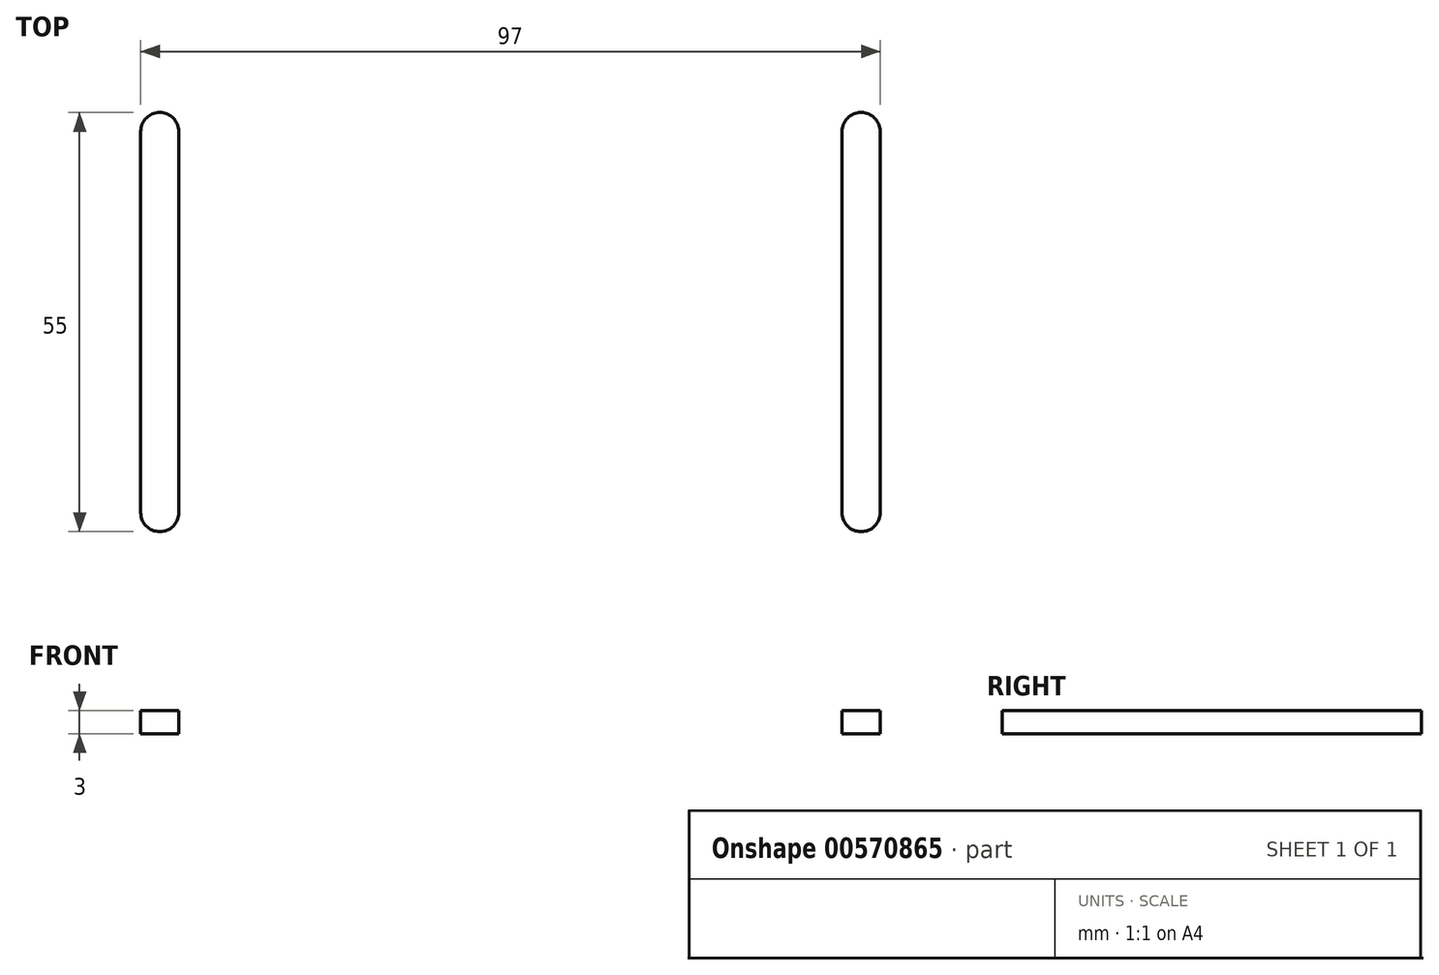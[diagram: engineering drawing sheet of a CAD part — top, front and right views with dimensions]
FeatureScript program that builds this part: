
annotation { "Feature Type Name" : "Feature", "Feature Type Description" : "" }
export const myFeature = defineFeature(function(context is Context, id is Id, definition is map)
    precondition{}
    {
        {
            var Q0;
            Q0=qCreatedBy(makeId("Top.planeOp"),FACE);
            var sketch = newSketch(context, id + "F0", { "sketchPlane" : qUnion([Q0])});
            skLineSegment(sketch, "E0.bottom", {"start": v(0, 0) * mm, "end": v(56, 0) * mm});
            skLineSegment(sketch, "E0.top", {"start": v(0, 145) * mm, "end": v(56, 145) * mm});
            skLineSegment(sketch, "E0.left", {"start": v(0, 0) * mm, "end": v(0, 145) * mm});
            skLineSegment(sketch, "E0.right", {"start": v(56, 0) * mm, "end": v(56, 145) * mm});
            skSolve(sketch);
        }
        {
            var Q0;
            Q0=makeQuery(id+"F0.imprint","IMPRINT",FACE,{"disambiguationData":[TD([[makeQuery(id+"F0.imprint","IMPRINT",EDGE,{"derivedFrom":sQuery(id+"F0.wireOp",EDGE,"E0.bottom")}),1.0]])]});
            extrude(context, id + "F1", {"entities" : qUnion([Q0]), "depth" : 3 * mm, "offsetDistance" : 25 * mm});
        }
        {
            var Q0;
            Q0=makeQuery(id+"F1.opExtrude","CAP_FACE",FACE,{"disambiguationData":[OSD([sQuery(id+"F0.wireOp",EDGE,"E0.bottom"),sQuery(id+"F0.wireOp",EDGE,"E0.top"),sQuery(id+"F0.wireOp",EDGE,"E0.left"),sQuery(id+"F0.wireOp",EDGE,"E0.right")])],"isStart":false});
            var sketch = newSketch(context, id + "F2", { "sketchPlane" : qUnion([Q0])});
            skLineSegment(sketch, "E1", {"start": v(25, 69) * mm, "end": v(25, 45) * mm});
            skSolve(sketch);
        }
        {
            var Q0;
            Q0=sQuery(id+"F2.wireOp",VERTEX,"E1.start");
            var Q1;
            Q1=sQuery(id+"F2.wireOp",VERTEX,"E1.end");
            var Q2;
            Q2=makeQuery(id+"F1.opExtrude","SWEPT_BODY",BODY,{"disambiguationData":[OSD([sQuery(id+"F0.wireOp",EDGE,"E0.bottom"),sQuery(id+"F0.wireOp",EDGE,"E0.top"),sQuery(id+"F0.wireOp",EDGE,"E0.left"),sQuery(id+"F0.wireOp",EDGE,"E0.right")])]});
            hole(context, id + "F3", {"style" : HoleStyle.SIMPLE, "endStyle" : HoleEndStyle.THROUGH, "holeDiameter" : 3 * mm, "isTappedThrough" : true, "tappedDepth" : 12 * mm, "tapClearance" : 3, "locations" : qUnion([Q0, Q1]), "scope" : qUnion([Q2])});
        }
        {
            var Q0;
            Q0=makeQuery(id+"F1.opExtrude","CAP_FACE",FACE,{"disambiguationData":[OSD([sQuery(id+"F0.wireOp",EDGE,"E0.bottom"),sQuery(id+"F0.wireOp",EDGE,"E0.top"),sQuery(id+"F0.wireOp",EDGE,"E0.left"),sQuery(id+"F0.wireOp",EDGE,"E0.right")])],"isStart":false});
            var sketch = newSketch(context, id + "F4", { "sketchPlane" : qUnion([Q0])});
            skLineSegment(sketch, "E2", {"start": v(36.35, 48.6) * mm, "end": v(36.35, 104.74) * mm});
            skSolve(sketch);
        }
        {
            var Q0;
            Q0=makeQuery(id+"F4.imprint","IMPRINT",FACE,{"disambiguationData":[TD([[makeQuery(id+"F4.imprint","IMPRINT",EDGE,{"derivedFrom":makeQuery(id+"F1.opExtrude","CAP_EDGE",EDGE,{"disambiguationData":[OSD([sQuery(id+"F0.wireOp",EDGE,"E0.bottom")])],"isStart":false})}),1.0]])]});
            var sketch = newSketch(context, id + "F5", { "sketchPlane" : qUnion([Q0])});
            skLineSegment(sketch, "E3", {"start": v(46, 82) * mm, "end": v(46, 32) * mm});
            skSolve(sketch);
        }
        {
            var Q0;
            Q0=makeQuery(id+"F5.imprint","IMPRINT",FACE,{"disambiguationData":[TD([[makeQuery(id+"F5.imprint","IMPRINT",EDGE,{"derivedFrom":makeQuery(id+"F4.imprint","IMPRINT",EDGE,{"derivedFrom":makeQuery(id+"F1.opExtrude","CAP_EDGE",EDGE,{"disambiguationData":[OSD([sQuery(id+"F0.wireOp",EDGE,"E0.bottom")])],"isStart":false})})}),1.0]])]});
            var sketch = newSketch(context, id + "F6", { "sketchPlane" : qUnion([Q0])});
            skSolve(sketch);
        }
        {
            var Q0;
            Q0=makeQuery(id+"F5.imprint","IMPRINT",FACE,{"disambiguationData":[TD([[makeQuery(id+"F5.imprint","IMPRINT",EDGE,{"derivedFrom":makeQuery(id+"F4.imprint","IMPRINT",EDGE,{"derivedFrom":makeQuery(id+"F1.opExtrude","CAP_EDGE",EDGE,{"disambiguationData":[OSD([sQuery(id+"F0.wireOp",EDGE,"E0.bottom")])],"isStart":false})})}),1.0]])]});
            var sketch = newSketch(context, id + "F7", { "sketchPlane" : qUnion([Q0])});
            skLineSegment(sketch, "E4.JWB.JWB", {"start": v(46, 82) * mm, "end": v(46, 32) * mm, "construction": true});
            skArc(sketch, "E4.0.startCap", {"start": v(43.5, 82) * mm, "mid": v(46, 84.5) * mm, "end": v(48.5, 82) * mm});
            skArc(sketch, "E4.0.endCap", {"start": v(48.5, 32) * mm, "mid": v(46, 29.5) * mm, "end": v(43.5, 32) * mm});
            skLineSegment(sketch, "E4.0.left", {"start": v(48.5, 82) * mm, "end": v(48.5, 32) * mm});
            skLineSegment(sketch, "E4.0.right", {"start": v(43.5, 82) * mm, "end": v(43.5, 32) * mm});
            skSolve(sketch);
        }
        {
            var Q0;
            Q0=makeQuery(id+"F7.imprint","IMPRINT",FACE,{"disambiguationData":[TD([[makeQuery(id+"F7.imprint","IMPRINT",EDGE,{"derivedFrom":sQuery(id+"F7.wireOp",EDGE,"E4.0.startCap")}),-1.0]])]});
            extrude(context, id + "F8", {"entities" : qUnion([Q0]), "operationType" : NewBodyOperationType.REMOVE, "oppositeDirection" : true, "depth" : 25 * mm, "offsetDistance" : 25 * mm});
        }
        {
            var Q0;
            Q0=makeQuery(id+"F6.imprint","IMPRINT",FACE,{"disambiguationData":[TD([[makeQuery(id+"F6.imprint","IMPRINT",EDGE,{"derivedFrom":makeQuery(id+"F5.imprint","IMPRINT",EDGE,{"derivedFrom":makeQuery(id+"F4.imprint","IMPRINT",EDGE,{"derivedFrom":makeQuery(id+"F1.opExtrude","CAP_EDGE",EDGE,{"disambiguationData":[OSD([sQuery(id+"F0.wireOp",EDGE,"E0.bottom")])],"isStart":false})})})}),1.0]])]});
            var sketch = newSketch(context, id + "F9", { "sketchPlane" : qUnion([Q0])});
            skSolve(sketch);
        }
        {
            var Q0;
            Q0=makeQuery(id+"F9.imprint","IMPRINT",FACE,{"disambiguationData":[TD([[makeQuery(id+"F9.imprint","IMPRINT",EDGE,{"derivedFrom":makeQuery(id+"F6.imprint","IMPRINT",EDGE,{"derivedFrom":makeQuery(id+"F5.imprint","IMPRINT",EDGE,{"derivedFrom":makeQuery(id+"F4.imprint","IMPRINT",EDGE,{"derivedFrom":makeQuery(id+"F1.opExtrude","CAP_EDGE",EDGE,{"disambiguationData":[OSD([sQuery(id+"F0.wireOp",EDGE,"E0.bottom")])],"isStart":false})})})})}),1.0]])]});
            var sketch = newSketch(context, id + "F10", { "sketchPlane" : qUnion([Q0])});
            skPoint(sketch, "E5", {"position": v(12, 133) * mm});
            skSolve(sketch);
        }
        {
            var Q0;
            Q0=sQuery(id+"F10.wireOp",VERTEX,"E5");
            var Q1;
            Q1=makeQuery(id+"F1.opExtrude","SWEPT_BODY",BODY,{"disambiguationData":[OSD([sQuery(id+"F0.wireOp",EDGE,"E0.bottom"),sQuery(id+"F0.wireOp",EDGE,"E0.top"),sQuery(id+"F0.wireOp",EDGE,"E0.left"),sQuery(id+"F0.wireOp",EDGE,"E0.right")])]});
            hole(context, id + "F11", {"style" : HoleStyle.SIMPLE, "endStyle" : HoleEndStyle.THROUGH, "holeDiameter" : 3 * mm, "isTappedThrough" : true, "tappedDepth" : 12 * mm, "tapClearance" : 3, "locations" : qUnion([Q0]), "scope" : qUnion([Q1])});
        }
        {
            var Q0;
            Q0=makeQuery(id+"F9.imprint","IMPRINT",FACE,{"disambiguationData":[TD([[makeQuery(id+"F9.imprint","IMPRINT",EDGE,{"derivedFrom":makeQuery(id+"F6.imprint","IMPRINT",EDGE,{"derivedFrom":makeQuery(id+"F5.imprint","IMPRINT",EDGE,{"derivedFrom":makeQuery(id+"F4.imprint","IMPRINT",EDGE,{"derivedFrom":makeQuery(id+"F1.opExtrude","CAP_EDGE",EDGE,{"disambiguationData":[OSD([sQuery(id+"F0.wireOp",EDGE,"E0.bottom")])],"isStart":false})})})})}),1.0]])]});
            var sketch = newSketch(context, id + "F12", { "sketchPlane" : qUnion([Q0])});
            skPoint(sketch, "E6", {"position": v(30, 22.5) * mm});
            skSolve(sketch);
        }
        {
            var Q0;
            Q0=sQuery(id+"F12.wireOp",VERTEX,"E6");
            var Q1;
            Q1=makeQuery(id+"F1.opExtrude","SWEPT_BODY",BODY,{"disambiguationData":[OSD([sQuery(id+"F0.wireOp",EDGE,"E0.bottom"),sQuery(id+"F0.wireOp",EDGE,"E0.top"),sQuery(id+"F0.wireOp",EDGE,"E0.left"),sQuery(id+"F0.wireOp",EDGE,"E0.right")])]});
            hole(context, id + "F13", {"style" : HoleStyle.SIMPLE, "endStyle" : HoleEndStyle.THROUGH, "holeDiameter" : 3 * mm, "isTappedThrough" : true, "tappedDepth" : 12 * mm, "tapClearance" : 3, "locations" : qUnion([Q0]), "scope" : qUnion([Q1])});
        }
        {
            var Q0;
            Q0=makeQuery(id+"F1.opExtrude","SWEPT_BODY",BODY,{"disambiguationData":[OSD([sQuery(id+"F0.wireOp",EDGE,"E0.bottom"),sQuery(id+"F0.wireOp",EDGE,"E0.top"),sQuery(id+"F0.wireOp",EDGE,"E0.left"),sQuery(id+"F0.wireOp",EDGE,"E0.right")])]});
            var Q1;
            Q1=qCreatedBy(makeId("Right.planeOp"),FACE);
            mirror(context, id + "F14", {"operationType" : NewBodyOperationType.ADD, "entities" : qUnion([Q0]), "mirrorPlane" : qUnion([Q1])});
        }
    });
